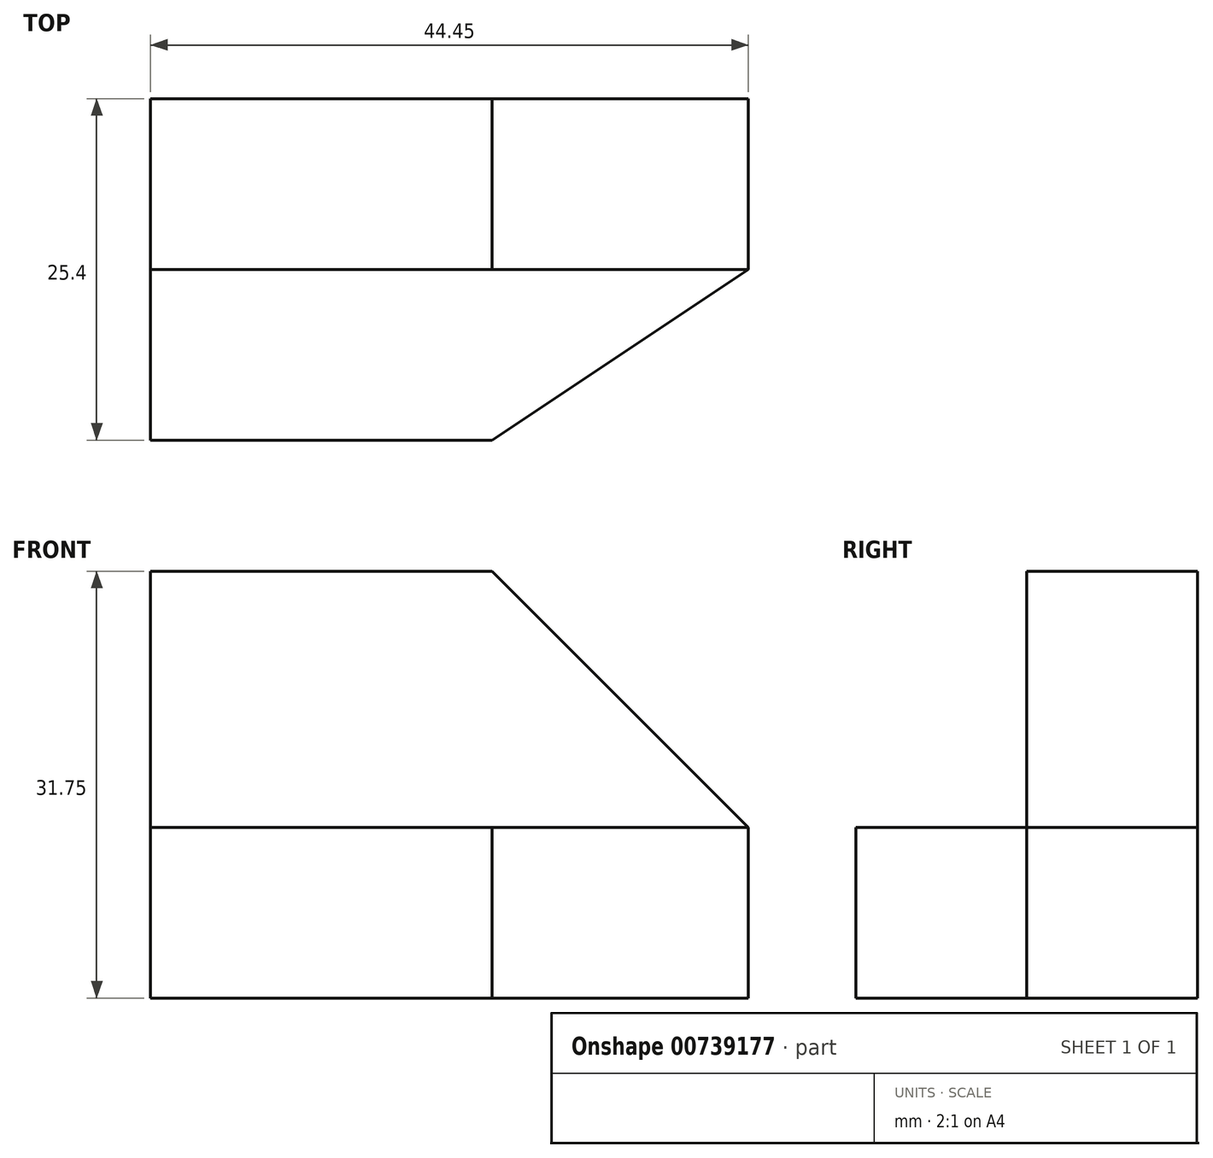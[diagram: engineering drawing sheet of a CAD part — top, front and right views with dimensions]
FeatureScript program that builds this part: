
annotation { "Feature Type Name" : "Feature", "Feature Type Description" : "" }
export const myFeature = defineFeature(function(context is Context, id is Id, definition is map)
    precondition{}
    {
        {
            var Q0;
            Q0=qCreatedBy(makeId("Front.planeOp"),FACE);
            var sketch = newSketch(context, id + "F0", { "sketchPlane" : qUnion([Q0])});
            skLineSegment(sketch, "E0", {"start": v(0, 31.75) * mm, "end": v(0, 0) * mm});
            skLineSegment(sketch, "E1", {"start": v(0, 0) * mm, "end": v(44.45, 0) * mm});
            skLineSegment(sketch, "E2", {"start": v(44.45, 0) * mm, "end": v(44.45, 31.75) * mm});
            skLineSegment(sketch, "E3", {"start": v(44.45, 31.75) * mm, "end": v(0, 31.75) * mm});
            skSolve(sketch);
        }
        {
            var Q0;
            Q0 = qSketchRegion(id + "F0", true);
            extrude(context, id + "F1", {"entities" : qUnion([Q0]), "depth" : 25.4 * mm, "offsetDistance" : 25.4 * mm});
        }
        {
            var Q0;
            Q0=makeQuery(id+"F1.opExtrude","CAP_FACE",FACE,{"disambiguationData":[OSD([sQuery(id+"F0.wireOp",EDGE,"E0"),sQuery(id+"F0.wireOp",EDGE,"E1"),sQuery(id+"F0.wireOp",EDGE,"E2"),sQuery(id+"F0.wireOp",EDGE,"E3")])],"isStart":false});
            var sketch = newSketch(context, id + "F2", { "sketchPlane" : qUnion([Q0])});
            skLineSegment(sketch, "E4", {"start": v(0, 12.7) * mm, "end": v(44.45, 12.7) * mm});
            skLineSegment(sketch, "E5", {"start": v(44.45, 12.7) * mm, "end": v(44.45, 0) * mm});
            skLineSegment(sketch, "E6", {"start": v(44.45, 0) * mm, "end": v(0, 0) * mm});
            skLineSegment(sketch, "E7", {"start": v(0, 0) * mm, "end": v(0, 12.7) * mm});
            skSolve(sketch);
        }
        {
            var Q0;
            {var subQ0=sQuery(id+"F2.wireOp",EDGE,"E4");Q0=makeQuery(id+"F2.imprint","IMPRINT",FACE,{"disambiguationData":[TD([[makeQuery(id+"F2.imprint","IMPRINT",EDGE,{"derivedFrom":subQ0}),1.0]])]});}
            extrude(context, id + "F3", {"entities" : qUnion([Q0]), "operationType" : NewBodyOperationType.REMOVE, "oppositeDirection" : true, "depth" : 12.7 * mm, "offsetDistance" : 25.4 * mm});
        }
        {
            var Q0;
            Q0=makeQuery(id+"F3.boolean.opBoolean","COPY",FACE,{"derivedFrom":makeQuery(id+"F3.opExtrude","CAP_FACE",FACE,{"disambiguationData":[OSD([sQuery(id+"F0.wireOp",EDGE,"E0"),sQuery(id+"F0.wireOp",EDGE,"E2"),sQuery(id+"F0.wireOp",EDGE,"E3"),sQuery(id+"F2.wireOp",EDGE,"E4")])],"isStart":false})});
            var sketch = newSketch(context, id + "F4", { "sketchPlane" : qUnion([Q0])});
            skLineSegment(sketch, "E8", {"start": v(25.4, 31.75) * mm, "end": v(44.45, 12.7) * mm});
            skSolve(sketch);
        }
        {
            var Q0;
            {var subQ0=sQuery(id+"F4.wireOp",EDGE,"E8");Q0=makeQuery(id+"F4.imprint","IMPRINT",FACE,{"disambiguationData":[TD([[makeQuery(id+"F4.imprint","IMPRINT",EDGE,{"derivedFrom":subQ0}),1.0]])]});}
            extrude(context, id + "F5", {"entities" : qUnion([Q0]), "operationType" : NewBodyOperationType.REMOVE, "endBound" : BoundingType.THROUGH_ALL, "oppositeDirection" : true, "depth" : 25.4 * mm, "offsetDistance" : 25.4 * mm});
        }
        {
            var Q0;
            Q0=makeQuery(id+"F3.boolean.opBoolean","COPY",FACE,{"derivedFrom":makeQuery(id+"F3.opExtrude","SWEPT_FACE",FACE,{"disambiguationData":[OSD([sQuery(id+"F2.wireOp",EDGE,"E4")])]})});
            var sketch = newSketch(context, id + "F6", { "sketchPlane" : qUnion([Q0])});
            skLineSegment(sketch, "E9", {"start": v(44.45, -12.7) * mm, "end": v(25.4, -25.4) * mm});
            skLineSegment(sketch, "E10", {"start": v(25.4, -25.4) * mm, "end": v(44.45, -25.4) * mm});
            skLineSegment(sketch, "E11", {"start": v(44.45, -25.4) * mm, "end": v(44.45, -12.7) * mm});
            skSolve(sketch);
        }
        {
            var Q0;
            Q0 = qSketchRegion(id + "F6", true);
            extrude(context, id + "F7", {"entities" : qUnion([Q0]), "operationType" : NewBodyOperationType.REMOVE, "endBound" : BoundingType.THROUGH_ALL, "oppositeDirection" : true, "depth" : 25.4 * mm, "offsetDistance" : 25.4 * mm});
        }
    });
